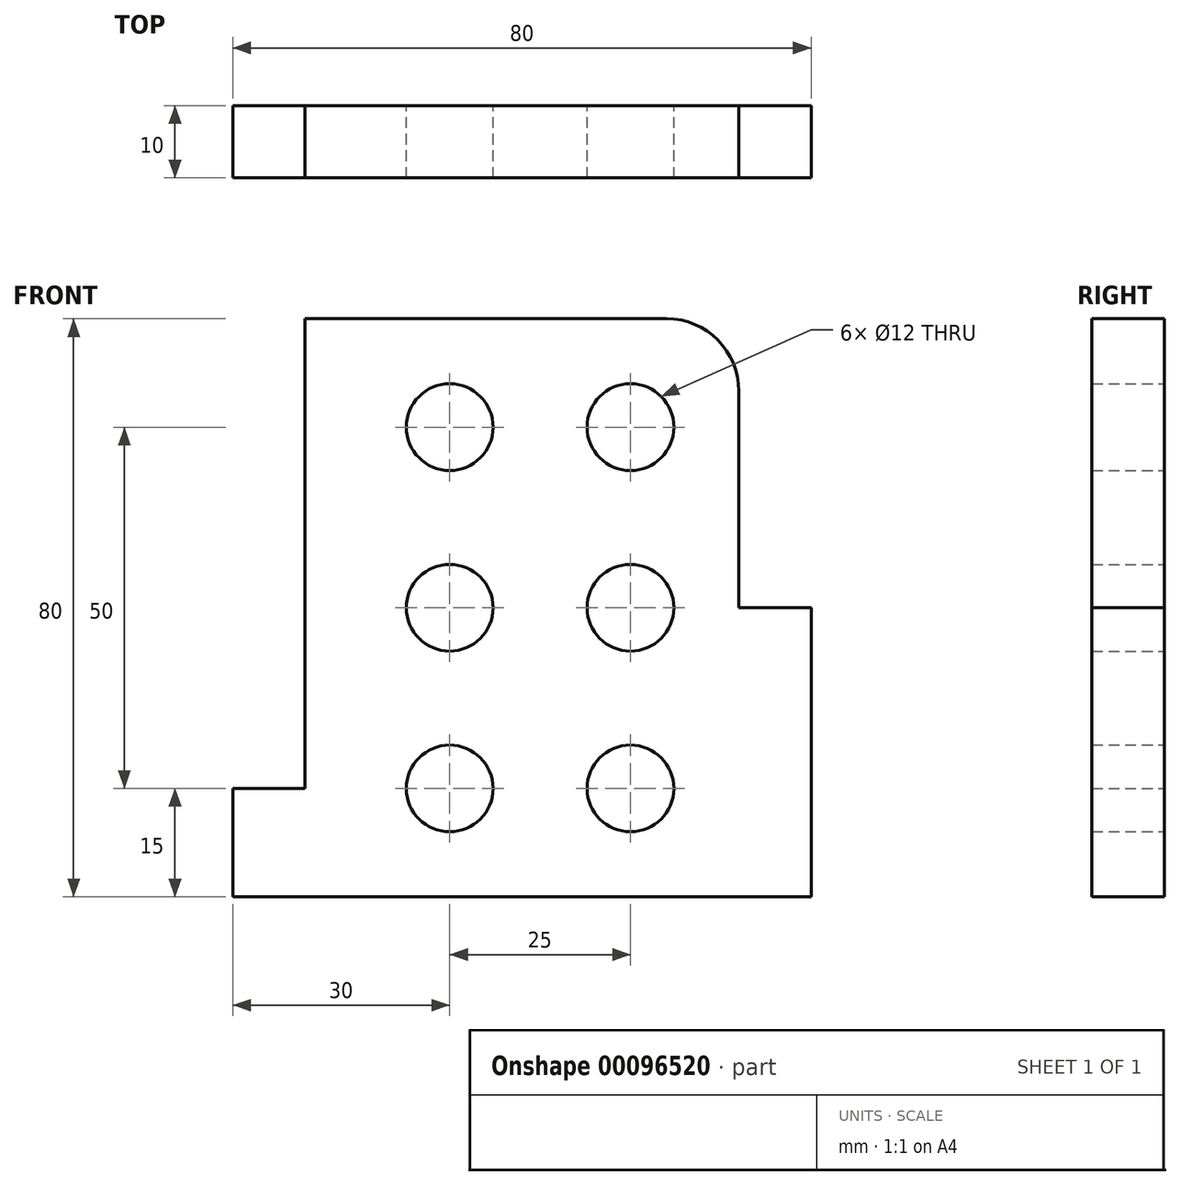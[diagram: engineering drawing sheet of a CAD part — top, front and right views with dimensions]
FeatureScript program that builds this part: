
annotation { "Feature Type Name" : "Feature", "Feature Type Description" : "" }
export const myFeature = defineFeature(function(context is Context, id is Id, definition is map)
    precondition{}
    {
        {
            var Q0;
            Q0=qCreatedBy(makeId("Front.planeOp"),FACE);
            var sketch = newSketch(context, id + "F0", { "sketchPlane" : qUnion([Q0])});
            skLineSegment(sketch, "E0", {"start": v(0, 0) * mm, "end": v(80, 0) * mm});
            skLineSegment(sketch, "E1", {"start": v(80, 0) * mm, "end": v(80, 40) * mm});
            skLineSegment(sketch, "E2", {"start": v(0, 0) * mm, "end": v(0, 15) * mm});
            skLineSegment(sketch, "E3", {"start": v(0, 15) * mm, "end": v(10, 15) * mm});
            skLineSegment(sketch, "E4", {"start": v(10, 15) * mm, "end": v(10, 80) * mm});
            skLineSegment(sketch, "E5", {"start": v(80, 40) * mm, "end": v(70, 40) * mm});
            skLineSegment(sketch, "E6", {"start": v(10, 80) * mm, "end": v(60, 80) * mm});
            skLineSegment(sketch, "E7", {"start": v(70, 70) * mm, "end": v(70, 40) * mm});
            skPoint(sketch, "E8.visualSharp", {"position": v(70, 80) * mm});
            skArc(sketch, "E8.filletArc", {"start": v(70, 70) * mm, "mid": v(67.07, 77.07) * mm, "end": v(60, 80) * mm});
            skCircle(sketch, "E9", {"center": v(30, 15) * mm, "radius": 6 * mm});
            skPoint(sketch, "E9.centerSnap0", {"position": v(5, 15) * mm});
            skCircle(sketch, "E10", {"center": v(55, 15) * mm, "radius": 6 * mm});
            skCircle(sketch, "E11", {"center": v(30, 40) * mm, "radius": 6 * mm});
            skCircle(sketch, "E12", {"center": v(55, 40) * mm, "radius": 6 * mm});
            skCircle(sketch, "E13", {"center": v(30, 65) * mm, "radius": 6 * mm});
            skCircle(sketch, "E14", {"center": v(55, 65) * mm, "radius": 6 * mm});
            skSolve(sketch);
        }
        {
            var Q0;
            Q0 = qSketchRegion(id + "F0", true);
            extrude(context, id + "F1", {"entities" : qUnion([Q0]), "depth" : 10 * mm});
        }
    });
